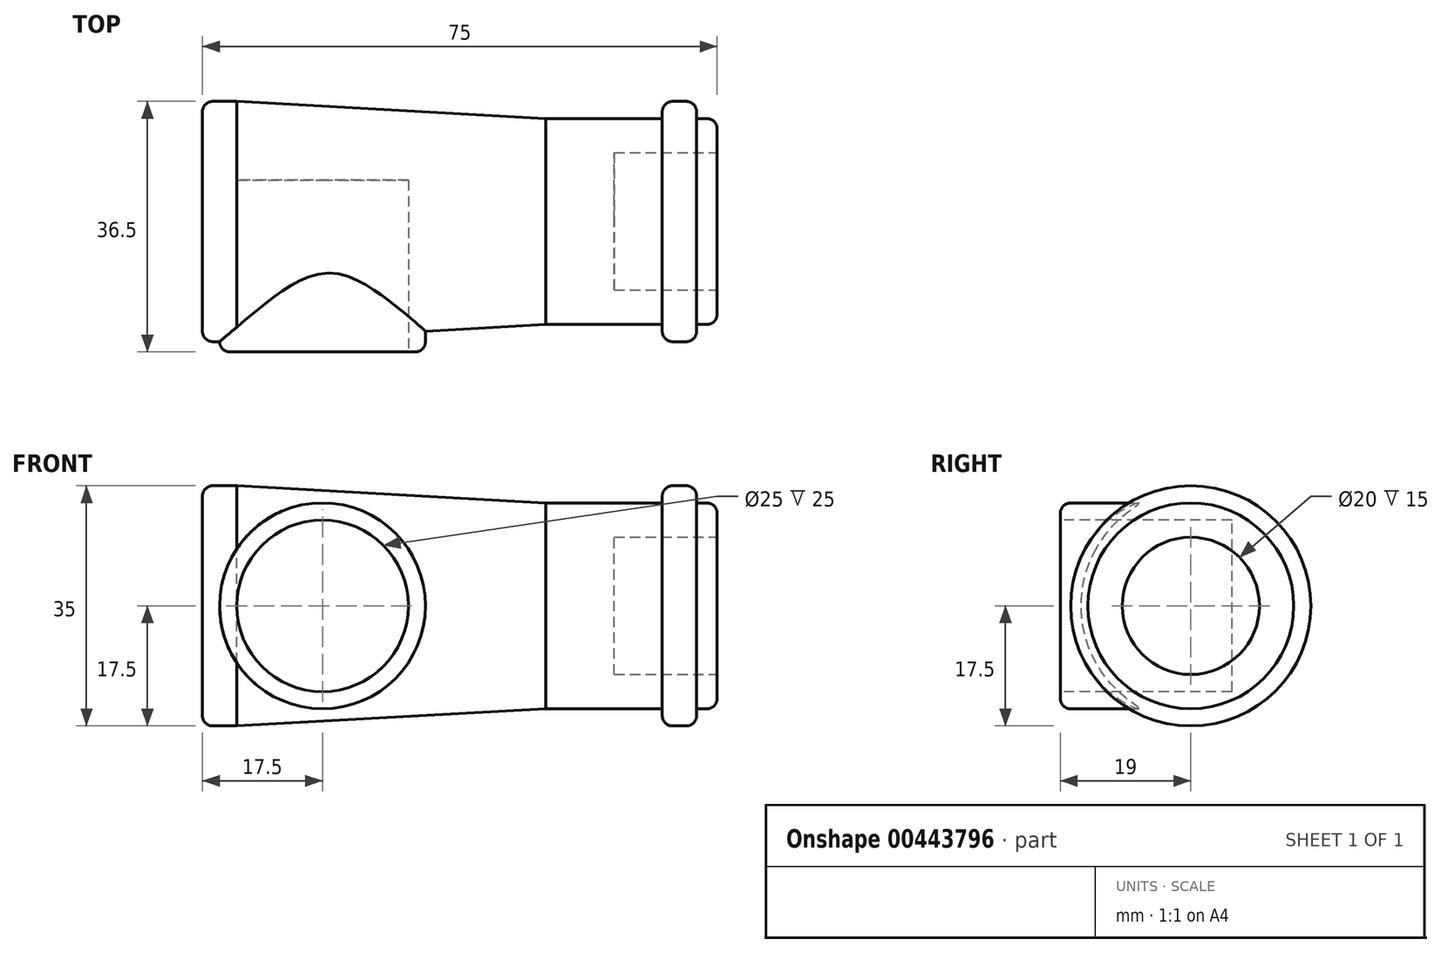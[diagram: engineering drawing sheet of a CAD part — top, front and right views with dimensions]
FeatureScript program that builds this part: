
annotation { "Feature Type Name" : "Feature", "Feature Type Description" : "" }
export const myFeature = defineFeature(function(context is Context, id is Id, definition is map)
    precondition{}
    {
        {
            var Q0;
            Q0=qCreatedBy(makeId("Front.planeOp"),FACE);
            var sketch = newSketch(context, id + "F0", { "sketchPlane" : qUnion([Q0])});
            skLineSegment(sketch, "E0", {"start": v(0, 0) * mm, "end": v(0, 17.5) * mm});
            skLineSegment(sketch, "E1", {"start": v(0, 17.5) * mm, "end": v(5, 17.5) * mm});
            skLineSegment(sketch, "E2", {"start": v(5, 17.5) * mm, "end": v(50, 15) * mm});
            skLineSegment(sketch, "E3", {"start": v(50, 15) * mm, "end": v(67, 15) * mm});
            skLineSegment(sketch, "E4", {"start": v(67, 15) * mm, "end": v(67, 17.5) * mm});
            skLineSegment(sketch, "E5", {"start": v(67, 17.5) * mm, "end": v(72, 17.5) * mm});
            skLineSegment(sketch, "E6", {"start": v(72, 17.5) * mm, "end": v(72, 15) * mm});
            skLineSegment(sketch, "E7", {"start": v(72, 15) * mm, "end": v(75, 15) * mm});
            skLineSegment(sketch, "E8", {"start": v(75, 15) * mm, "end": v(75, 10) * mm});
            skLineSegment(sketch, "E9", {"start": v(75, 10) * mm, "end": v(60, 10) * mm});
            skLineSegment(sketch, "E10", {"start": v(60, 10) * mm, "end": v(60, 0) * mm});
            skLineSegment(sketch, "E11", {"start": v(60, 0) * mm, "end": v(0, 0) * mm});
            skSolve(sketch);
        }
        {
            var Q0;
            Q0 = qSketchRegion(id + "F0", true);
            var Q1;
            Q1=sQuery(id+"F0.wireOp",EDGE,"E11");
            revolve(context, id + "F1", {"entities" : qUnion([Q0]), "axis" : qUnion([Q1]), "revolveType" : RevolveType.FULL});
        }
        {
            var Q0;
            Q0=qCreatedBy(makeId("Front.planeOp"),FACE);
            var sketch = newSketch(context, id + "F2", { "sketchPlane" : qUnion([Q0])});
            skCircle(sketch, "E12", {"center": v(17.5, 0) * mm, "radius": 15 * mm});
            skSolve(sketch);
        }
        {
            var Q0;
            Q0 = qSketchRegion(id + "F2", true);
            extrude(context, id + "F3", {"entities" : qUnion([Q0]), "operationType" : NewBodyOperationType.ADD, "depth" : 19 * mm});
        }
        {
            var Q0;
            Q0=makeQuery(id+"F3.opExtrude","CAP_FACE",FACE,{"disambiguationData":[OSD([sQuery(id+"F2.wireOp",EDGE,"E12")])],"isStart":false});
            var sketch = newSketch(context, id + "F4", { "sketchPlane" : qUnion([Q0])});
            skCircle(sketch, "E13", {"center": v(17.5, 0) * mm, "radius": 12.5 * mm});
            skSolve(sketch);
        }
        {
            var Q0;
            Q0 = qSketchRegion(id + "F4", true);
            extrude(context, id + "F5", {"entities" : qUnion([Q0]), "operationType" : NewBodyOperationType.REMOVE, "oppositeDirection" : true, "depth" : 25 * mm});
        }
        {
            var Q0;
            Q0=makeQuery(id+"F1.opRevolve","SWEPT_EDGE",EDGE,{"disambiguationData":[OSD([sQuery(id+"F0.wireOp",EDGE,"E0"),sQuery(id+"F0.wireOp",EDGE,"E1")])]});
            var Q1;
            Q1=makeQuery(id+"F1.opRevolve","SWEPT_EDGE",EDGE,{"disambiguationData":[OSD([sQuery(id+"F0.wireOp",EDGE,"E4"),sQuery(id+"F0.wireOp",EDGE,"E5")])]});
            var Q2;
            Q2=makeQuery(id+"F1.opRevolve","SWEPT_EDGE",EDGE,{"disambiguationData":[OSD([sQuery(id+"F0.wireOp",EDGE,"E5"),sQuery(id+"F0.wireOp",EDGE,"E6")])]});
            var Q3;
            Q3=makeQuery(id+"F3.opExtrude","CAP_EDGE",EDGE,{"disambiguationData":[OSD([sQuery(id+"F2.wireOp",EDGE,"E12")])],"isStart":false});
            var Q4;
            Q4=makeQuery(id+"F1.opRevolve","SWEPT_EDGE",EDGE,{"disambiguationData":[OSD([sQuery(id+"F0.wireOp",EDGE,"E7"),sQuery(id+"F0.wireOp",EDGE,"E8")])]});
            fillet(context, id + "F6", {"entities" : qUnion([Q0, Q1, Q2, Q3, Q4]), "radius" : 1.5 * mm, "tangentPropagation" : true, "allowEdgeOverflow" : false});
        }
    });
